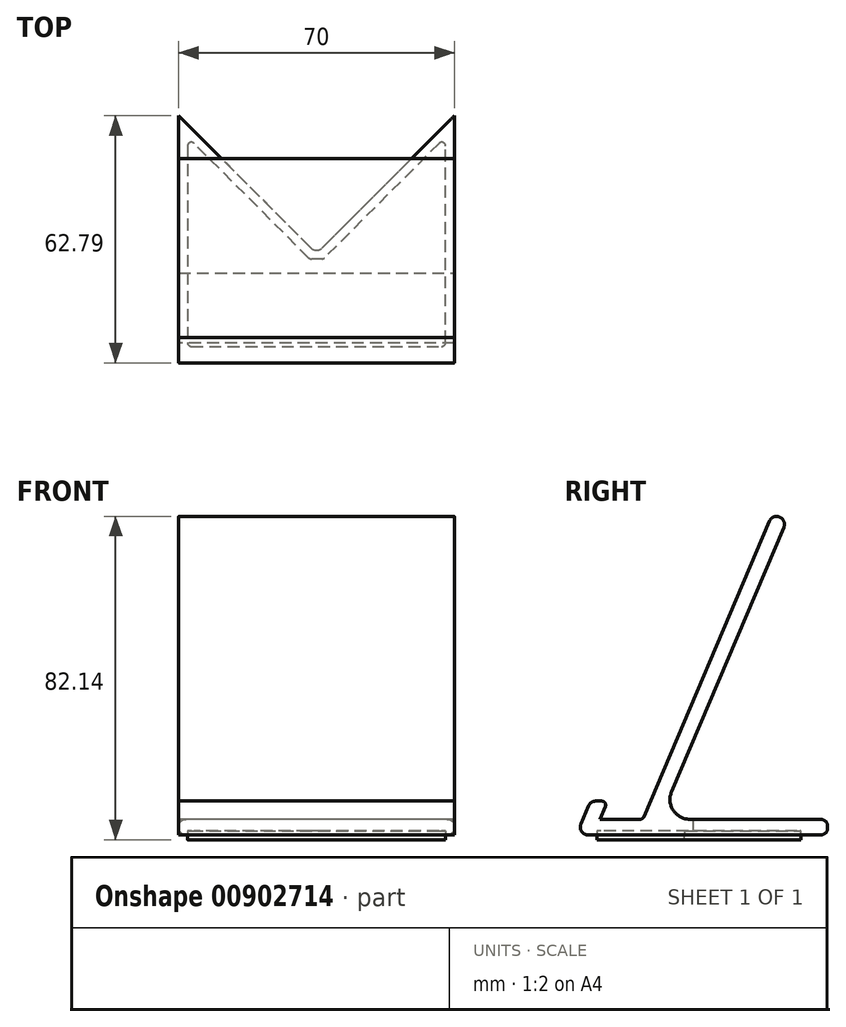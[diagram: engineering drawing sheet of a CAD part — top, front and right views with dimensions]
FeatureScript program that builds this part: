
annotation { "Feature Type Name" : "Feature", "Feature Type Description" : "" }
export const myFeature = defineFeature(function(context is Context, id is Id, definition is map)
    precondition{}
    {
        {
            var Q0;
            Q0=qCreatedBy(makeId("Right.planeOp"),FACE);
            var sketch = newSketch(context, id + "F0", { "sketchPlane" : qUnion([Q0])});
            skLineSegment(sketch, "E0", {"start": v(0, 0) * mm, "end": v(65, 0) * mm});
            skLineSegment(sketch, "E1", {"start": v(63.3, 4) * mm, "end": v(21.25, 4) * mm});
            skLineSegment(sketch, "E2", {"start": v(21.25, 4) * mm, "end": v(53.51, 80) * mm});
            skLineSegment(sketch, "E3", {"start": v(53.51, 80) * mm, "end": v(49.83, 81.56) * mm});
            skLineSegment(sketch, "E4", {"start": v(49.83, 81.56) * mm, "end": v(16.9, 4) * mm});
            skLineSegment(sketch, "E5", {"start": v(16.9, 4) * mm, "end": v(6.04, 4) * mm});
            skLineSegment(sketch, "E6", {"start": v(6.04, 4) * mm, "end": v(8, 8.6) * mm});
            skLineSegment(sketch, "E7", {"start": v(8, 8.6) * mm, "end": v(3.65, 8.6) * mm});
            skLineSegment(sketch, "E8", {"start": v(3.65, 8.6) * mm, "end": v(0, 0) * mm});
            skLineSegment(sketch, "E9", {"start": v(49.83, 81.56) * mm, "end": v(53.51, 80) * mm, "construction": true});
            skLineSegment(sketch, "E10", {"start": v(21.25, 4) * mm, "end": v(21.25, 0) * mm, "construction": true});
            skLineSegment(sketch, "E11", {"start": v(8, 8.6) * mm, "end": v(17.2, 4.7) * mm, "construction": true});
            skLineSegment(sketch, "E12", {"start": v(3.65, 8.6) * mm, "end": v(7.33, 7.04) * mm, "construction": true});
            skLineSegment(sketch, "E13", {"start": v(65, 0) * mm, "end": v(63.3, 4) * mm});
            skSolve(sketch);
        }
        {
            var Q0;
            Q0 = qSketchRegion(id + "F0", true);
            extrude(context, id + "F1", {"entities" : qUnion([Q0]), "depth" : 70 * mm, "offsetDistance" : 25 * mm});
        }
        {
            var Q0;
            Q0=makeQuery(id+"F1.opExtrude","SWEPT_EDGE",EDGE,{"disambiguationData":[OSD([sQuery(id+"F0.wireOp",EDGE,"E3"),sQuery(id+"F0.wireOp",EDGE,"E4")])]});
            var Q1;
            Q1=makeQuery(id+"F1.opExtrude","SWEPT_EDGE",EDGE,{"disambiguationData":[OSD([sQuery(id+"F0.wireOp",EDGE,"E2"),sQuery(id+"F0.wireOp",EDGE,"E3")])]});
            var Q2;
            Q2=makeQuery(id+"F1.opExtrude","SWEPT_EDGE",EDGE,{"disambiguationData":[OSD([sQuery(id+"F0.wireOp",EDGE,"E7"),sQuery(id+"F0.wireOp",EDGE,"E8")])]});
            var Q3;
            Q3=makeQuery(id+"F1.opExtrude","SWEPT_EDGE",EDGE,{"disambiguationData":[OSD([sQuery(id+"F0.wireOp",EDGE,"E0"),sQuery(id+"F0.wireOp",EDGE,"E8")])]});
            var Q4;
            Q4=makeQuery(id+"F1.opExtrude","SWEPT_EDGE",EDGE,{"disambiguationData":[OSD([sQuery(id+"F0.wireOp",EDGE,"E0"),sQuery(id+"F0.wireOp",EDGE,"E13")])]});
            var Q5;
            Q5=makeQuery(id+"F1.opExtrude","SWEPT_EDGE",EDGE,{"disambiguationData":[OSD([sQuery(id+"F0.wireOp",EDGE,"E1"),sQuery(id+"F0.wireOp",EDGE,"E13")])]});
            fillet(context, id + "F2", {"entities" : qUnion([Q0, Q1, Q2, Q3, Q4, Q5]), "radius" : 2 * mm, "tangentPropagation" : true, "allowEdgeOverflow" : false});
        }
        {
            var Q0;
            Q0=makeQuery(id+"F1.opExtrude","SWEPT_EDGE",EDGE,{"disambiguationData":[OSD([sQuery(id+"F0.wireOp",EDGE,"E6"),sQuery(id+"F0.wireOp",EDGE,"E7")])]});
            var Q1;
            Q1=makeQuery(id+"F1.opExtrude","SWEPT_EDGE",EDGE,{"disambiguationData":[OSD([sQuery(id+"F0.wireOp",EDGE,"E4"),sQuery(id+"F0.wireOp",EDGE,"E5")])]});
            fillet(context, id + "F3", {"entities" : qUnion([Q0, Q1]), "radius" : 1 * mm, "tangentPropagation" : true, "allowEdgeOverflow" : false});
        }
        {
            var Q0;
            Q0=makeQuery(id+"F1.opExtrude","SWEPT_EDGE",EDGE,{"disambiguationData":[OSD([sQuery(id+"F0.wireOp",EDGE,"E1"),sQuery(id+"F0.wireOp",EDGE,"E2")])]});
            fillet(context, id + "F4", {"entities" : qUnion([Q0]), "radius" : 5 * mm, "tangentPropagation" : true, "allowEdgeOverflow" : false});
        }
        {
            var Q0;
            Q0=makeQuery(id+"F1.opExtrude","SWEPT_FACE",FACE,{"disambiguationData":[OSD([sQuery(id+"F0.wireOp",EDGE,"E1")])]});
            var sketch = newSketch(context, id + "F5", { "sketchPlane" : qUnion([Q0])});
            skLineSegment(sketch, "E14", {"start": v(35, 61.98) * mm, "end": v(35, 28.8) * mm, "construction": true});
            skLineSegment(sketch, "E15", {"start": v(35, 28.8) * mm, "end": v(68.17, 61.98) * mm});
            skLineSegment(sketch, "E16", {"start": v(35, 28.8) * mm, "end": v(1.83, 61.98) * mm});
            skLineSegment(sketch, "E17", {"start": v(1.83, 61.98) * mm, "end": v(-0.17, 63.98) * mm});
            skLineSegment(sketch, "E18", {"start": v(-0.17, 63.98) * mm, "end": v(70.17, 63.98) * mm});
            skLineSegment(sketch, "E19", {"start": v(70.17, 63.98) * mm, "end": v(68.17, 61.98) * mm});
            skSolve(sketch);
        }
        {
            var Q0;
            Q0 = qSketchRegion(id + "F5", true);
            extrude(context, id + "F6", {"entities" : qUnion([Q0]), "operationType" : NewBodyOperationType.REMOVE, "endBound" : BoundingType.UP_TO_NEXT, "oppositeDirection" : true, "depth" : 25 * mm, "offsetDistance" : 25 * mm});
        }
        {
            var Q0;
            Q0=makeQuery(id+"F6.boolean.opBoolean","COPY",EDGE,{"derivedFrom":makeQuery(id+"F6.opExtrude","SWEPT_EDGE",EDGE,{"disambiguationData":[OSD([sQuery(id+"F0.wireOp",EDGE,"E1"),sQuery(id+"F0.wireOp",EDGE,"E2"),sQuery(id+"F5.wireOp",EDGE,"E15"),sQuery(id+"F5.wireOp",EDGE,"E16")])]})});
            fillet(context, id + "F7", {"entities" : qUnion([Q0]), "radius" : 2 * mm, "tangentPropagation" : true, "allowEdgeOverflow" : false});
        }
        {
            var Q0;
            Q0=makeQuery(id+"F1.opExtrude","SWEPT_FACE",FACE,{"disambiguationData":[OSD([sQuery(id+"F0.wireOp",EDGE,"E0")])]});
            var sketch = newSketch(context, id + "F8", { "sketchPlane" : qUnion([Q0])});
            skLineSegment(sketch, "E20", {"start": v(2.2, -5.22) * mm, "end": v(67.8, -5.22) * mm});
            skLineSegment(sketch, "E21", {"start": v(67.8, -5.22) * mm, "end": v(67.8, -58.5) * mm});
            skLineSegment(sketch, "E22", {"start": v(67.8, -58.5) * mm, "end": v(36.74, -27.43) * mm});
            skLineSegment(sketch, "E23", {"start": v(36.74, -27.43) * mm, "end": v(33.26, -27.43) * mm});
            skLineSegment(sketch, "E24", {"start": v(33.26, -27.43) * mm, "end": v(2.2, -58.5) * mm});
            skLineSegment(sketch, "E25", {"start": v(2.2, -58.5) * mm, "end": v(2.2, -5.22) * mm});
            skLineSegment(sketch, "E26", {"start": v(2.2, -5.22) * mm, "end": v(0, -5.22) * mm, "construction": true});
            skLineSegment(sketch, "E27", {"start": v(2.2, -5.22) * mm, "end": v(2.2, -3.02) * mm, "construction": true});
            skLineSegment(sketch, "E28", {"start": v(67.8, -58.5) * mm, "end": v(66.24, -60.05) * mm, "construction": true});
            skLineSegment(sketch, "E29", {"start": v(35, -27.43) * mm, "end": v(35, -29.63) * mm, "construction": true});
            skLineSegment(sketch, "E30", {"start": v(2.2, -58.5) * mm, "end": v(3.76, -60.05) * mm, "construction": true});
            skLineSegment(sketch, "E31", {"start": v(67.8, -5.22) * mm, "end": v(70, -5.22) * mm, "construction": true});
            skLineSegment(sketch, "E32", {"start": v(1.56, -59.78) * mm, "end": v(1.56, -61.98) * mm, "construction": true});
            skPoint(sketch, "E32.endSnap0", {"position": v(0.91, -61.98) * mm});
            skLineSegment(sketch, "E33", {"start": v(68.44, -59.78) * mm, "end": v(68.44, -61.98) * mm, "construction": true});
            skSolve(sketch);
        }
        {
            var Q0;
            Q0 = qSketchRegion(id + "F8", true);
            extrude(context, id + "F9", {"entities" : qUnion([Q0]), "operationType" : NewBodyOperationType.REMOVE, "oppositeDirection" : true, "depth" : 1 * mm, "offsetDistance" : 25 * mm});
        }
        {
            var Q0;
            Q0 = qSketchRegion(id + "F8", true);
            extrude(context, id + "F10", {"entities" : qUnion([Q0]), "depth" : 1.2 * mm, "offsetDistance" : 25 * mm});
        }
        {
            var Q0;
            Q0=makeQuery(id+"F10.opExtrude","SWEPT_EDGE",EDGE,{"disambiguationData":[OSD([sQuery(id+"F8.wireOp",EDGE,"E20"),sQuery(id+"F8.wireOp",EDGE,"E25")])]});
            var Q1;
            Q1=makeQuery(id+"F10.opExtrude","SWEPT_EDGE",EDGE,{"disambiguationData":[OSD([sQuery(id+"F8.wireOp",EDGE,"JptKYPtp-OCt6-bDrD-KwB2-aUvmv9NMXCMJ"),sQuery(id+"F8.wireOp",EDGE,"E25")])]});
            var Q2;
            Q2=makeQuery(id+"F10.opExtrude","SWEPT_EDGE",EDGE,{"disambiguationData":[OSD([sQuery(id+"F8.wireOp",EDGE,"E24"),sQuery(id+"F8.wireOp",EDGE,"JptKYPtp-OCt6-bDrD-KwB2-aUvmv9NMXCMJ")])]});
            var Q3;
            Q3=makeQuery(id+"F10.opExtrude","SWEPT_EDGE",EDGE,{"disambiguationData":[OSD([sQuery(id+"F8.wireOp",EDGE,"E23"),sQuery(id+"F8.wireOp",EDGE,"E24")])]});
            var Q4;
            Q4=makeQuery(id+"F10.opExtrude","SWEPT_EDGE",EDGE,{"disambiguationData":[OSD([sQuery(id+"F8.wireOp",EDGE,"E22"),sQuery(id+"F8.wireOp",EDGE,"E23")])]});
            var Q5;
            Q5=makeQuery(id+"F10.opExtrude","SWEPT_EDGE",EDGE,{"disambiguationData":[OSD([sQuery(id+"F8.wireOp",EDGE,"L9dONhCX-yAvx-J163-oc2F-fSdcQ3GZ6uVY"),sQuery(id+"F8.wireOp",EDGE,"E22")])]});
            var Q6;
            Q6=makeQuery(id+"F10.opExtrude","SWEPT_EDGE",EDGE,{"disambiguationData":[OSD([sQuery(id+"F8.wireOp",EDGE,"E21"),sQuery(id+"F8.wireOp",EDGE,"L9dONhCX-yAvx-J163-oc2F-fSdcQ3GZ6uVY")])]});
            var Q7;
            Q7=makeQuery(id+"F10.opExtrude","SWEPT_EDGE",EDGE,{"disambiguationData":[OSD([sQuery(id+"F8.wireOp",EDGE,"E20"),sQuery(id+"F8.wireOp",EDGE,"E21")])]});
            fillet(context, id + "F11", {"entities" : qUnion([Q0, Q1, Q2, Q3, Q4, Q5, Q6, Q7]), "radius" : 1 * mm, "tangentPropagation" : true, "allowEdgeOverflow" : false});
        }
        {
            var Q0;
            Q0=makeQuery(id+"F9.boolean.opBoolean","COPY",EDGE,{"derivedFrom":makeQuery(id+"F9.opExtrude","SWEPT_EDGE",EDGE,{"disambiguationData":[OSD([sQuery(id+"F8.wireOp",EDGE,"E20"),sQuery(id+"F8.wireOp",EDGE,"E25")])]})});
            var Q1;
            Q1=makeQuery(id+"F9.boolean.opBoolean","COPY",EDGE,{"derivedFrom":makeQuery(id+"F9.opExtrude","SWEPT_EDGE",EDGE,{"disambiguationData":[OSD([sQuery(id+"F8.wireOp",EDGE,"E20"),sQuery(id+"F8.wireOp",EDGE,"E21")])]})});
            var Q2;
            Q2=makeQuery(id+"F9.boolean.opBoolean","COPY",EDGE,{"derivedFrom":makeQuery(id+"F9.opExtrude","SWEPT_EDGE",EDGE,{"disambiguationData":[OSD([sQuery(id+"F8.wireOp",EDGE,"E21"),sQuery(id+"F8.wireOp",EDGE,"L9dONhCX-yAvx-J163-oc2F-fSdcQ3GZ6uVY")])]})});
            var Q3;
            Q3=makeQuery(id+"F9.boolean.opBoolean","COPY",EDGE,{"derivedFrom":makeQuery(id+"F9.opExtrude","SWEPT_EDGE",EDGE,{"disambiguationData":[OSD([sQuery(id+"F8.wireOp",EDGE,"L9dONhCX-yAvx-J163-oc2F-fSdcQ3GZ6uVY"),sQuery(id+"F8.wireOp",EDGE,"E22")])]})});
            var Q4;
            Q4=makeQuery(id+"F9.boolean.opBoolean","COPY",EDGE,{"derivedFrom":makeQuery(id+"F9.opExtrude","SWEPT_EDGE",EDGE,{"disambiguationData":[OSD([sQuery(id+"F8.wireOp",EDGE,"JptKYPtp-OCt6-bDrD-KwB2-aUvmv9NMXCMJ"),sQuery(id+"F8.wireOp",EDGE,"E25")])]})});
            var Q5;
            Q5=makeQuery(id+"F9.boolean.opBoolean","COPY",EDGE,{"derivedFrom":makeQuery(id+"F9.opExtrude","SWEPT_EDGE",EDGE,{"disambiguationData":[OSD([sQuery(id+"F8.wireOp",EDGE,"E24"),sQuery(id+"F8.wireOp",EDGE,"JptKYPtp-OCt6-bDrD-KwB2-aUvmv9NMXCMJ")])]})});
            var Q6;
            Q6=makeQuery(id+"F9.boolean.opBoolean","COPY",EDGE,{"derivedFrom":makeQuery(id+"F9.opExtrude","SWEPT_EDGE",EDGE,{"disambiguationData":[OSD([sQuery(id+"F8.wireOp",EDGE,"E23"),sQuery(id+"F8.wireOp",EDGE,"E24")])]})});
            var Q7;
            Q7=makeQuery(id+"F9.boolean.opBoolean","COPY",EDGE,{"derivedFrom":makeQuery(id+"F9.opExtrude","SWEPT_EDGE",EDGE,{"disambiguationData":[OSD([sQuery(id+"F8.wireOp",EDGE,"E22"),sQuery(id+"F8.wireOp",EDGE,"E23")])]})});
            fillet(context, id + "F12", {"entities" : qUnion([Q0, Q1, Q2, Q3, Q4, Q5, Q6, Q7]), "radius" : 1 * mm, "tangentPropagation" : true, "allowEdgeOverflow" : false});
        }
    });
